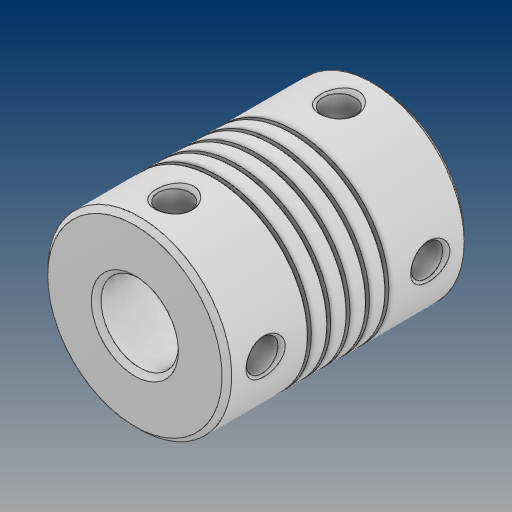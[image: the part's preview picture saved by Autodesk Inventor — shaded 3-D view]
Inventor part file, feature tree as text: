
AUTODESK INVENTOR PART (.ipt)
format: ipt  version: 2021 (Build 250183000, 183)  size: 408,064 bytes
history: native  units: mm
features: mirror x1
ambient origin geometry x8: Origin, YZ Plane, XZ Plane, XY Plane, X Axis, Y Axis, Z Axis, Center Point
bodies: Solid1 (feature_tree)
feature tree (1):
  mirror  "Mirror1"
